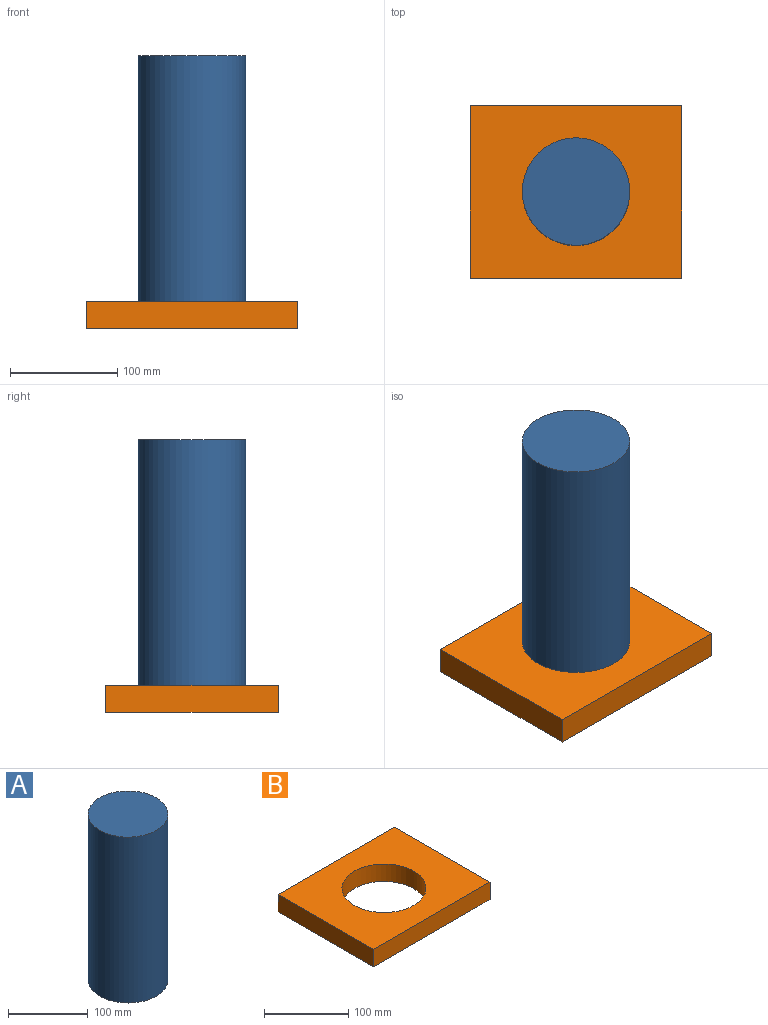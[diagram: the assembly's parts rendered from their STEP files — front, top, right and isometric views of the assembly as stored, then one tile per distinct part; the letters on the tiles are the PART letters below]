
ASSEMBLY  parts=2 mates=1
PART A: 3 faces, bbox 100x100x254 mm
  f0: cylinder r=50mm len=254mm, axis (0,0,-1), area 79796.5mm2, adj f1,f2
  f1: plane 100x100mm, normal (0,0,1), area 7854mm2, adj f0
  f2: plane 100x100mm, normal (0,0,-1), area 7854mm2, adj f0
PART B: 7 faces, bbox 196.5x160.3x25.4 mm
  f0: plane 196.5x25.4mm, normal (0,-1,0), area 4991mm2, adj f1,f4,f5,f6
  f1: plane 160.32x25.4mm, normal (1,0,0), area 4072.2mm2, adj f0,f2,f5,f6
  f2: plane 196.5x25.4mm, normal (0,1,0), area 4991mm2, adj f1,f4,f5,f6
  f3: cylinder r=50mm len=100mm, axis (0,0,-1), area 7979.6mm2, adj f5,f6
  f4: plane 160.32x25.4mm, normal (-1,0,0), area 4072.2mm2, adj f0,f2,f5,f6
  f5: plane 196.5x160.32mm, normal (0,0,1), area 23648.7mm2, adj f0,f1,f2,f3,f4
  f6: plane 196.5x160.32mm, normal (0,0,-1), area 23648.7mm2, adj f0,f1,f2,f3,f4
PLACE A t=(16.09,54.88,55.68)mm
PLACE B t=(16.09,54.88,55.68)mm
MATE slider A.f0 <-> B.f3  axis (0,0,-1) through (16.09,54.88,55.68)mm
